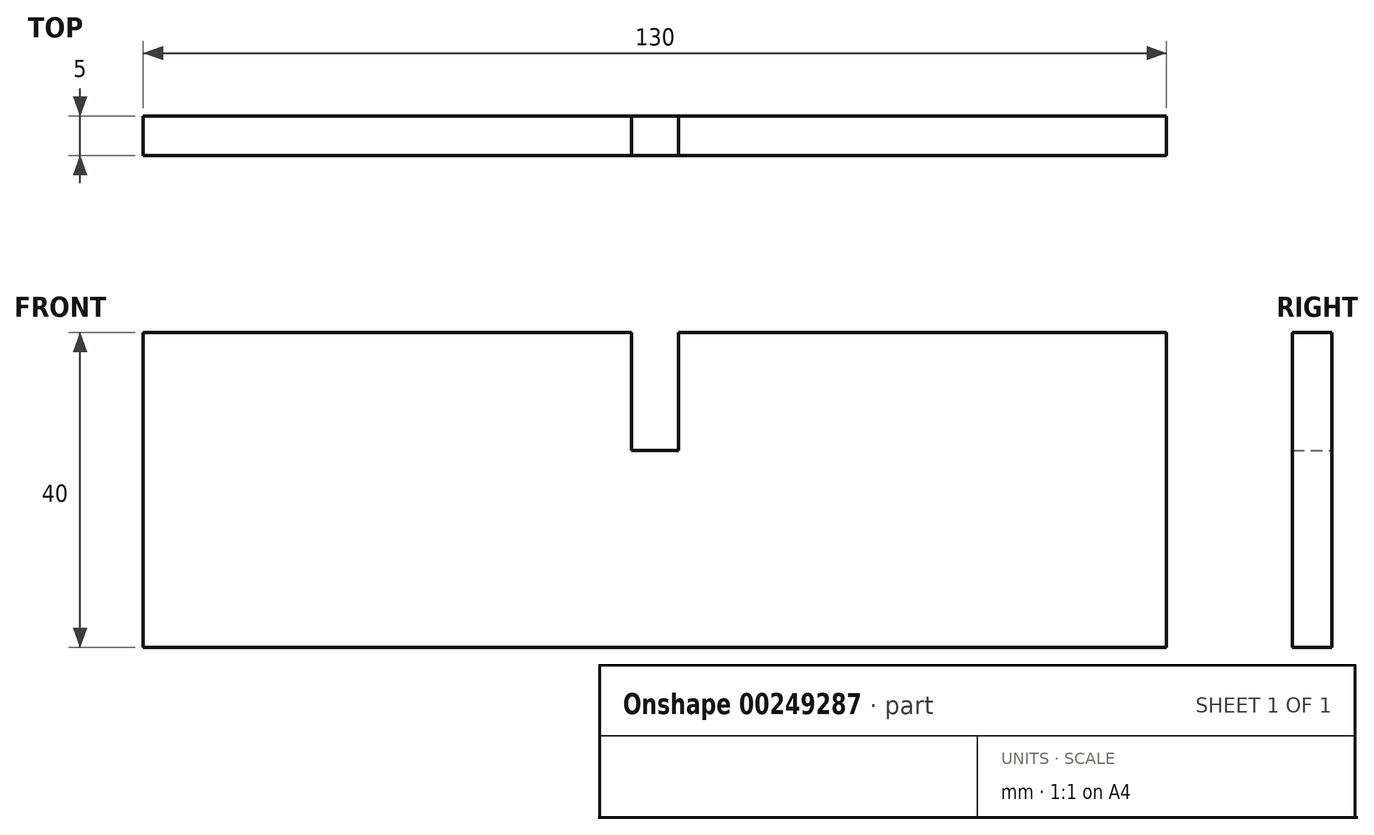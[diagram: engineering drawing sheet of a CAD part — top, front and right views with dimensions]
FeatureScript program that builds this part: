
annotation { "Feature Type Name" : "Feature", "Feature Type Description" : "" }
export const myFeature = defineFeature(function(context is Context, id is Id, definition is map)
    precondition{}
    {
        {
            var Q0;
            Q0=qCreatedBy(makeId("Front.planeOp"),FACE);
            var sketch = newSketch(context, id + "F0", { "sketchPlane" : qUnion([Q0])});
            skLineSegment(sketch, "E0", {"start": v(-65, 0) * mm, "end": v(-3, 0) * mm});
            skLineSegment(sketch, "E1", {"start": v(65, 0) * mm, "end": v(65, -40) * mm});
            skLineSegment(sketch, "E2", {"start": v(65, -40) * mm, "end": v(-65, -40) * mm});
            skLineSegment(sketch, "E3", {"start": v(-65, 0) * mm, "end": v(-65, -40) * mm});
            skLineSegment(sketch, "E4", {"start": v(-3, 0) * mm, "end": v(-3, -15) * mm});
            skLineSegment(sketch, "E5", {"start": v(-3, -15) * mm, "end": v(3, -15) * mm});
            skLineSegment(sketch, "E6", {"start": v(3, -15) * mm, "end": v(3, 0) * mm});
            skLineSegment(sketch, "E7.trimOffspring", {"start": v(3, 0) * mm, "end": v(65, 0) * mm});
            skSolve(sketch);
        }
        {
            var Q0;
            Q0 = qSketchRegion(id + "F0", true);
            extrude(context, id + "F1", {"entities" : qUnion([Q0]), "depth" : 5 * mm, "offsetDistance" : 25 * mm, "symmetric" : true});
        }
    });
